SOLIDWORKS PART (.sldprt)
format: sldprt  version: not decoded by parser v0  size: 221,696 bytes
history: native  units: mm
features: plane x6, sketch x4, material x1, extrude x1, cut_extrude x1, pattern_circular x1, fillet x1 (+9 scaffold rows collapsed)
feature tree (24):
  scaffold x9  (default folders/planes/origin — collapsed)
  material  "Materiale <non specificato>"
  plane  "Frontale"
  plane  "Superiore"
  plane  "Destro"
  sketch  "Schizzo1"  dims[D1=35.0mm]
  extrude  "Estrusione-Estrusione1"  Depth=9mm
  plane  "Piano1"  Offset=16mm
  plane  "Piano2"  Offset=13mm
  sketch  "Schizzo4"  dims[c1.D1=0.4mm c1.D2=0.4mm c1.D3=3.4mm c1.D4=3.4mm c2.D1=5.0mm c2.D2=5.0mm c2.D3=1.1mm c2.D4=1.1mm]
  sketch  "Schizzo5"
  plane  "Piano3"  Offset=12mm
  sketch  "Schizzo9"  dims[c1.D4=50.5mm c1.D1=1.0mm c1.D2=~19.762067mm c2.D1=20.0mm c2.D2=2.5mm c2.D3=1.5mm c3.D1=22.0mm c3.D2=2.8mm c3.D3=2.8mm c3.D4=1.5mm c3.D5=23.0mm c3.D6=26.5mm c3.D7=27.5mm c4.D5=~8.524309mm c4.D6=~1.475691mm c5.D5=23.0mm c5.D6=26.5mm c5.D7=27.5mm c6.D5=~8.524309mm c6.D6=~1.475691mm c7.D5=~1.475691mm]
  cut_extrude  "Taglio-Estrusione2"  Depth=25mm
  pattern_circular  "RipetizioneCircolare7"  Count=7 Angle=51.428571deg
  fillet  "Raccordo1"  Radius=1.5mm
decode coverage: 7 of 8 modeling features carry decoded parameters
note: ~ marks probable driven/reference dimensions
note: suppression state not decoded; provenance and decode notes live in map.json
